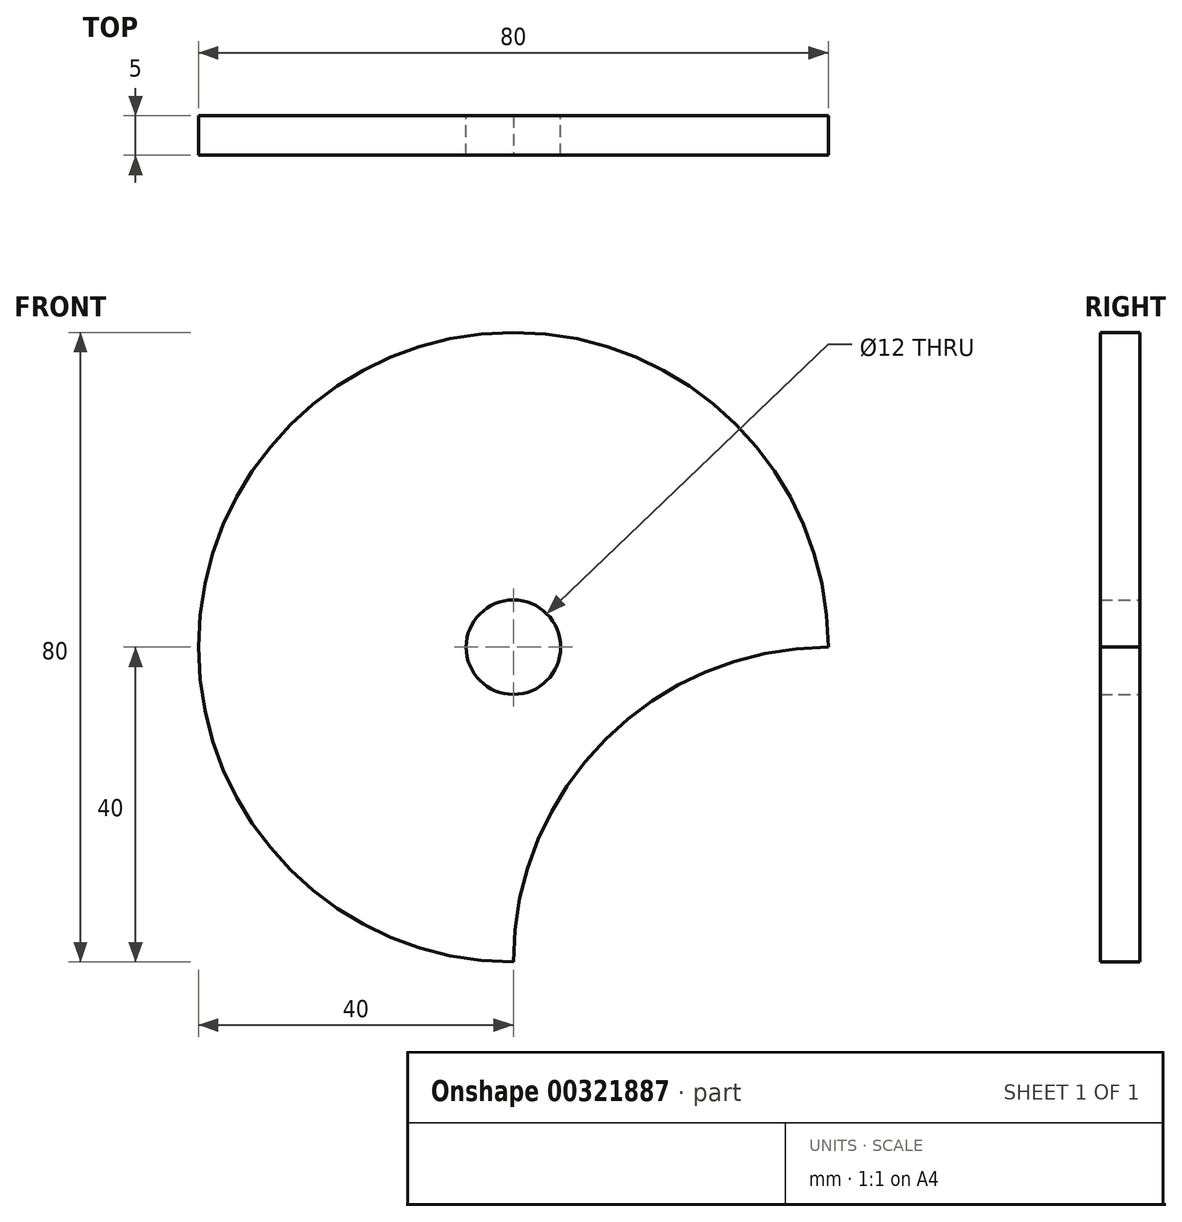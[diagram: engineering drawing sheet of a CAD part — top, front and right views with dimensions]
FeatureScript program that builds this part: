
annotation { "Feature Type Name" : "Feature", "Feature Type Description" : "" }
export const myFeature = defineFeature(function(context is Context, id is Id, definition is map)
    precondition{}
    {
        {
            var Q0;
            Q0=qCreatedBy(makeId("Front.planeOp"),FACE);
            var sketch = newSketch(context, id + "F0", { "sketchPlane" : qUnion([Q0])});
            skCircle(sketch, "E0", {"center": v(0, 0) * mm, "radius": 40 * mm});
            skCircle(sketch, "E1", {"center": v(0, 0) * mm, "radius": 6 * mm});
            skSolve(sketch);
        }
        {
            var Q0;
            Q0 = qSketchRegion(id + "F0", true);
            extrude(context, id + "F1", {"entities" : qUnion([Q0]), "depth" : 5 * mm});
        }
        {
            var Q0;
            Q0=makeQuery(id+"F1.opExtrude","CAP_FACE",FACE,{"disambiguationData":[OSD([sQuery(id+"F0.wireOp",EDGE,"E0"),sQuery(id+"F0.wireOp",EDGE,"E1")])],"isStart":false});
            var sketch = newSketch(context, id + "F2", { "sketchPlane" : qUnion([Q0])});
            skLineSegment(sketch, "E2", {"start": v(0, 0) * mm, "end": v(65.72, -65.72) * mm, "construction": true});
            skArc(sketch, "E3", {"start": v(40, 0) * mm, "mid": v(11.72, -11.72) * mm, "end": v(0, -40) * mm});
            skArc(sketch, "E4.0", {"start": v(0, -40) * mm, "mid": v(28.28, -28.28) * mm, "end": v(40, 0) * mm});
            skSolve(sketch);
        }
        {
            var Q0;
            Q0 = qSketchRegion(id + "F2", true);
            extrude(context, id + "F3", {"entities" : qUnion([Q0]), "operationType" : NewBodyOperationType.REMOVE, "oppositeDirection" : true, "depth" : 25 * mm});
        }
    });
